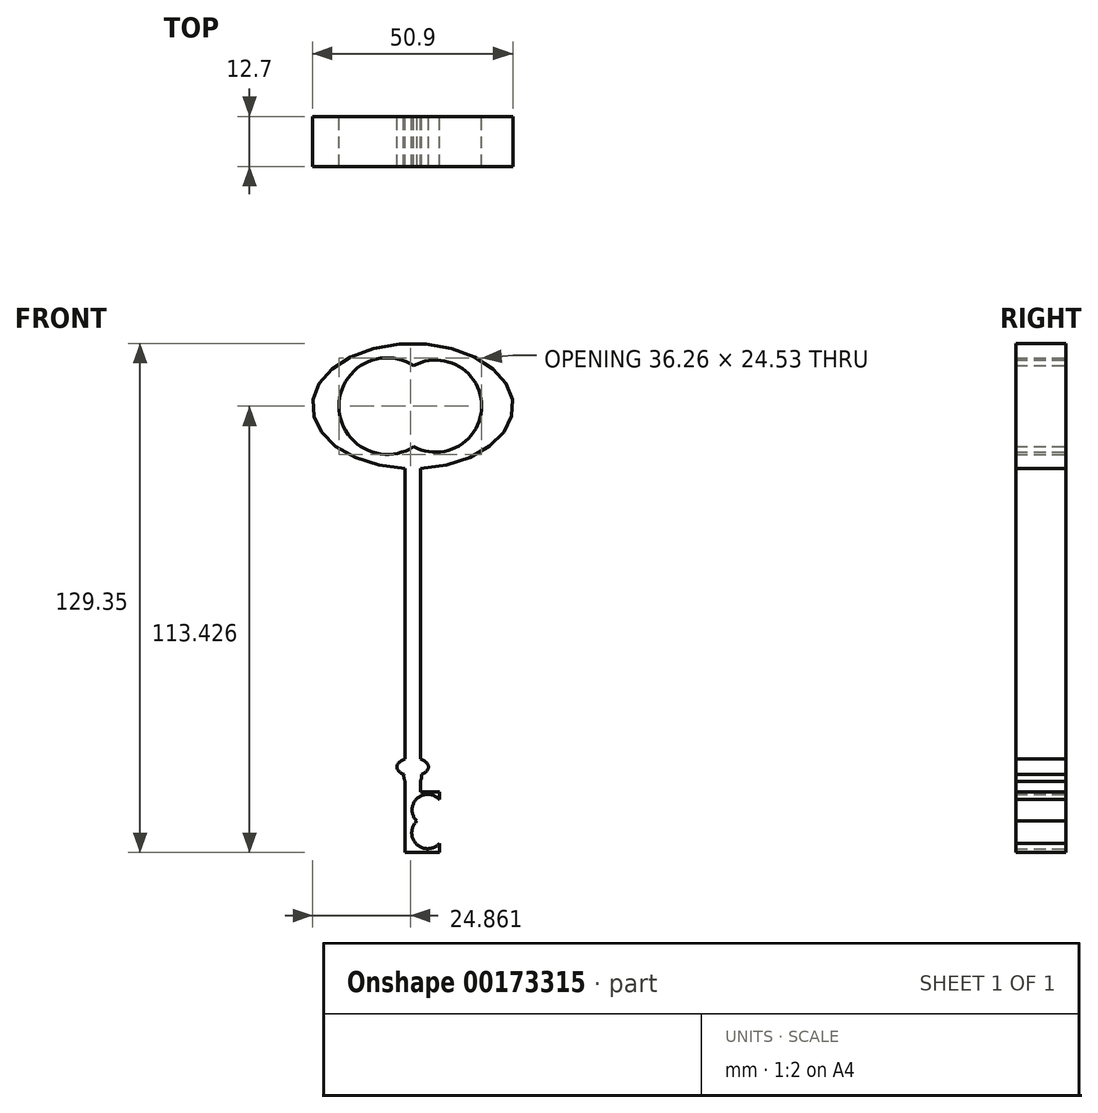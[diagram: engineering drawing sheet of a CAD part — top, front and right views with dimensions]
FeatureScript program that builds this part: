
annotation { "Feature Type Name" : "Feature", "Feature Type Description" : "" }
export const myFeature = defineFeature(function(context is Context, id is Id, definition is map)
    precondition{}
    {
        {
            var Q0;
            Q0=qCreatedBy(makeId("Front.planeOp"),FACE);
            var sketch = newSketch(context, id + "F0", { "sketchPlane" : qUnion([Q0])});
            skEllipse(sketch, "E0", {"center": v(0, 35.93) * mm, "majorRadius": 25.45 * mm, "minorRadius": 15.92 * mm, "majorAxis": v(-1, 0)});
            skCircle(sketch, "E1", {"center": v(-6.44, 35.93) * mm, "radius": 12.28 * mm});
            skCircle(sketch, "E2", {"center": v(5.83, 35.93) * mm, "radius": 11.7 * mm});
            skLineSegment(sketch, "E3", {"start": v(1.94, 20.05) * mm, "end": v(1.94, -55.75) * mm});
            skLineSegment(sketch, "E4", {"start": v(1.94, -55.75) * mm, "end": v(-1.9, -55.75) * mm});
            skLineSegment(sketch, "E5", {"start": v(-1.9, -55.75) * mm, "end": v(-1.9, 20.05) * mm});
            skEllipse(sketch, "E6", {"center": v(0, -55.75) * mm, "majorRadius": 3.98 * mm, "minorRadius": 2.29 * mm, "majorAxis": v(1, 0)});
            skEllipse(sketch, "E7", {"center": v(0, -58.04) * mm, "majorRadius": 2.57 * mm, "minorRadius": 2.27 * mm, "majorAxis": v(0, -1)});
            skLineSegment(sketch, "E8", {"start": v(-1.9, -55.75) * mm, "end": v(-1.9, -62.14) * mm});
            skLineSegment(sketch, "E9", {"start": v(1.94, -62.14) * mm, "end": v(1.94, -55.75) * mm});
            skLineSegment(sketch, "E10", {"start": v(1.94, -62.08) * mm, "end": v(6.76, -62.08) * mm});
            skLineSegment(sketch, "E11", {"start": v(6.76, -62.08) * mm, "end": v(6.76, -62.14) * mm});
            skLineSegment(sketch, "E12", {"start": v(-1.9, -62.14) * mm, "end": v(-1.9, -77.5) * mm});
            skLineSegment(sketch, "E13", {"start": v(-1.9, -77.5) * mm, "end": v(6.76, -77.5) * mm});
            skLineSegment(sketch, "E14", {"start": v(6.76, -77.5) * mm, "end": v(6.76, -62.14) * mm});
            skCircle(sketch, "E15", {"center": v(3.8, -66.65) * mm, "radius": 3.96 * mm});
            skCircle(sketch, "E16", {"center": v(3.8, -72.47) * mm, "radius": 4.04 * mm});
            skSolve(sketch);
        }
        {
            var Q0;
            {var subQ0=sQuery(id+"F0.wireOp",EDGE,"E3");var subQ1=sQuery(id+"F0.wireOp",EDGE,"E0");var subQ2=makeQuery(id+"F0.imprint","INTERSECT",VERTEX,{"derivedFrom":[subQ1,subQ0]});Q0=makeQuery(id+"F0.imprint","IMPRINT",FACE,{"disambiguationData":[TD([[makeQuery(id+"F0.imprint","IMPRINT",EDGE,{"disambiguationData":[TD([[subQ2,1.0]])],"derivedFrom":subQ1}),-1.0]])]});}
            var Q1;
            {var subQ1=sQuery(id+"F0.wireOp",EDGE,"E3");var subQ3=sQuery(id+"F0.wireOp",EDGE,"E6");var subQ4=makeQuery(id+"F0.imprint","INTERSECT",VERTEX,{"derivedFrom":[subQ1,subQ3]});Q1=makeQuery(id+"F0.imprint","IMPRINT",FACE,{"disambiguationData":[TD([[makeQuery(id+"F0.imprint","IMPRINT",EDGE,{"disambiguationData":[TD([[subQ4,1.0]])],"derivedFrom":subQ3}),1.0]])]});}
            var Q2;
            {var subQ3=sQuery(id+"F0.wireOp",EDGE,"E6");var subQ7=sQuery(id+"F0.wireOp",EDGE,"E3");var subQ10=makeQuery(id+"F0.imprint","INTERSECT",VERTEX,{"derivedFrom":[subQ7,subQ3]});Q2=makeQuery(id+"F0.imprint","IMPRINT",FACE,{"disambiguationData":[TD([[makeQuery(id+"F0.imprint","IMPRINT",EDGE,{"disambiguationData":[TD([[subQ10,-1.0]])],"derivedFrom":subQ3}),1.0]])]});}
            var Q3;
            {var subQ1=sQuery(id+"F0.wireOp",EDGE,"E5");var subQ3=sQuery(id+"F0.wireOp",EDGE,"E6");var subQ4=makeQuery(id+"F0.imprint","INTERSECT",VERTEX,{"derivedFrom":[subQ1,subQ3]});Q3=makeQuery(id+"F0.imprint","IMPRINT",FACE,{"disambiguationData":[TD([[makeQuery(id+"F0.imprint","IMPRINT",EDGE,{"disambiguationData":[TD([[subQ4,-1.0]])],"derivedFrom":subQ3}),1.0]])]});}
            var Q4;
            {var subQ1=sQuery(id+"F0.wireOp",EDGE,"E4");var subQ3=sQuery(id+"F0.wireOp",EDGE,"E7");var subQ4=makeQuery(id+"F0.imprint","INTERSECT",VERTEX,{"disambiguationData":[OD(1.0)],"derivedFrom":[subQ1,subQ3]});Q4=makeQuery(id+"F0.imprint","IMPRINT",FACE,{"disambiguationData":[TD([[makeQuery(id+"F0.imprint","IMPRINT",EDGE,{"disambiguationData":[TD([[subQ4,-1.0]])],"derivedFrom":subQ3}),-1.0]])]});}
            var Q5;
            {var subQ0=sQuery(id+"F0.wireOp",EDGE,"E7");var subQ1=sQuery(id+"F0.wireOp",EDGE,"E4");var subQ2=makeQuery(id+"F0.imprint","INTERSECT",VERTEX,{"disambiguationData":[OD(0.0)],"derivedFrom":[subQ1,subQ0]});Q5=makeQuery(id+"F0.imprint","IMPRINT",FACE,{"disambiguationData":[TD([[makeQuery(id+"F0.imprint","IMPRINT",EDGE,{"disambiguationData":[TD([[subQ2,-1.0]])],"derivedFrom":subQ1}),-1.0]])]});}
            var Q6;
            {var subQ1=sQuery(id+"F0.wireOp",EDGE,"E4");var subQ3=sQuery(id+"F0.wireOp",EDGE,"E7");var subQ4=makeQuery(id+"F0.imprint","INTERSECT",VERTEX,{"disambiguationData":[OD(0.0)],"derivedFrom":[subQ1,subQ3]});Q6=makeQuery(id+"F0.imprint","IMPRINT",FACE,{"disambiguationData":[TD([[makeQuery(id+"F0.imprint","IMPRINT",EDGE,{"disambiguationData":[TD([[subQ4,1.0]])],"derivedFrom":subQ3}),-1.0]])]});}
            var Q7;
            {var subQ0=sQuery(id+"F0.wireOp",EDGE,"E7");var subQ1=sQuery(id+"F0.wireOp",EDGE,"E6");var subQ2=makeQuery(id+"F0.imprint","INTERSECT",VERTEX,{"disambiguationData":[OD(0.0)],"derivedFrom":[subQ1,subQ0]});Q7=makeQuery(id+"F0.imprint","IMPRINT",FACE,{"disambiguationData":[TD([[makeQuery(id+"F0.imprint","IMPRINT",EDGE,{"disambiguationData":[TD([[subQ2,-1.0]])],"derivedFrom":subQ1}),1.0]])]});}
            var Q8;
            {var subQ0=sQuery(id+"F0.wireOp",EDGE,"E8");var subQ1=sQuery(id+"F0.wireOp",EDGE,"E6");var subQ2=makeQuery(id+"F0.imprint","INTERSECT",VERTEX,{"derivedFrom":[subQ1,subQ0]});Q8=makeQuery(id+"F0.imprint","IMPRINT",FACE,{"disambiguationData":[TD([[makeQuery(id+"F0.imprint","IMPRINT",EDGE,{"disambiguationData":[TD([[subQ2,-1.0]])],"derivedFrom":subQ1}),-1.0]])]});}
            var Q9;
            {var subQ0=sQuery(id+"F0.wireOp",EDGE,"E7");var subQ1=sQuery(id+"F0.wireOp",EDGE,"E6");var subQ2=makeQuery(id+"F0.imprint","INTERSECT",VERTEX,{"disambiguationData":[OD(1.0)],"derivedFrom":[subQ1,subQ0]});Q9=makeQuery(id+"F0.imprint","IMPRINT",FACE,{"disambiguationData":[TD([[makeQuery(id+"F0.imprint","IMPRINT",EDGE,{"disambiguationData":[TD([[subQ2,1.0]])],"derivedFrom":subQ1}),1.0]])]});}
            var Q10;
            {var subQ0=sQuery(id+"F0.wireOp",EDGE,"E7");var subQ1=sQuery(id+"F0.wireOp",EDGE,"E4");var subQ2=makeQuery(id+"F0.imprint","INTERSECT",VERTEX,{"disambiguationData":[OD(0.0)],"derivedFrom":[subQ1,subQ0]});Q10=makeQuery(id+"F0.imprint","IMPRINT",FACE,{"disambiguationData":[TD([[makeQuery(id+"F0.imprint","IMPRINT",EDGE,{"disambiguationData":[TD([[subQ2,-1.0]])],"derivedFrom":subQ1}),1.0]])]});}
            var Q11;
            {var subQ0=sQuery(id+"F0.wireOp",EDGE,"E7");var subQ1=sQuery(id+"F0.wireOp",EDGE,"E6");var subQ2=makeQuery(id+"F0.imprint","INTERSECT",VERTEX,{"disambiguationData":[OD(1.0)],"derivedFrom":[subQ1,subQ0]});Q11=makeQuery(id+"F0.imprint","IMPRINT",FACE,{"disambiguationData":[TD([[makeQuery(id+"F0.imprint","IMPRINT",EDGE,{"disambiguationData":[TD([[subQ2,1.0]])],"derivedFrom":subQ1}),-1.0]])]});}
            var Q12;
            {var subQ0=sQuery(id+"F0.wireOp",EDGE,"E7");var subQ1=sQuery(id+"F0.wireOp",EDGE,"E6");var subQ2=makeQuery(id+"F0.imprint","INTERSECT",VERTEX,{"disambiguationData":[OD(0.0)],"derivedFrom":[subQ1,subQ0]});Q12=makeQuery(id+"F0.imprint","IMPRINT",FACE,{"disambiguationData":[TD([[makeQuery(id+"F0.imprint","IMPRINT",EDGE,{"disambiguationData":[TD([[subQ2,-1.0]])],"derivedFrom":subQ1}),-1.0]])]});}
            var Q13;
            {var subQ13=sQuery(id+"F0.wireOp",EDGE,"E10");Q13=makeQuery(id+"F0.imprint","IMPRINT",FACE,{"disambiguationData":[TD([[makeQuery(id+"F0.imprint","IMPRINT",EDGE,{"derivedFrom":subQ13}),-1.0]])]});}
            var Q14;
            {var subQ0=sQuery(id+"F0.wireOp",EDGE,"E0");var subQ1=makeQuery(id+"F0.imprint","INTERSECT",VERTEX,{"derivedFrom":[subQ0,sQuery(id+"F0.wireOp",EDGE,"E3")]});Q14=makeQuery(id+"F0.imprint","IMPRINT",FACE,{"disambiguationData":[TD([[makeQuery(id+"F0.imprint","IMPRINT",EDGE,{"disambiguationData":[TD([[subQ1,1.0]])],"derivedFrom":subQ0}),1.0]])]});}
            extrude(context, id + "F1", {"entities" : qUnion([Q0, Q1, Q2, Q3, Q4, Q5, Q6, Q7, Q8, Q9, Q10, Q11, Q12, Q13, Q14]), "depth" : 12.7 * mm});
        }
    });
